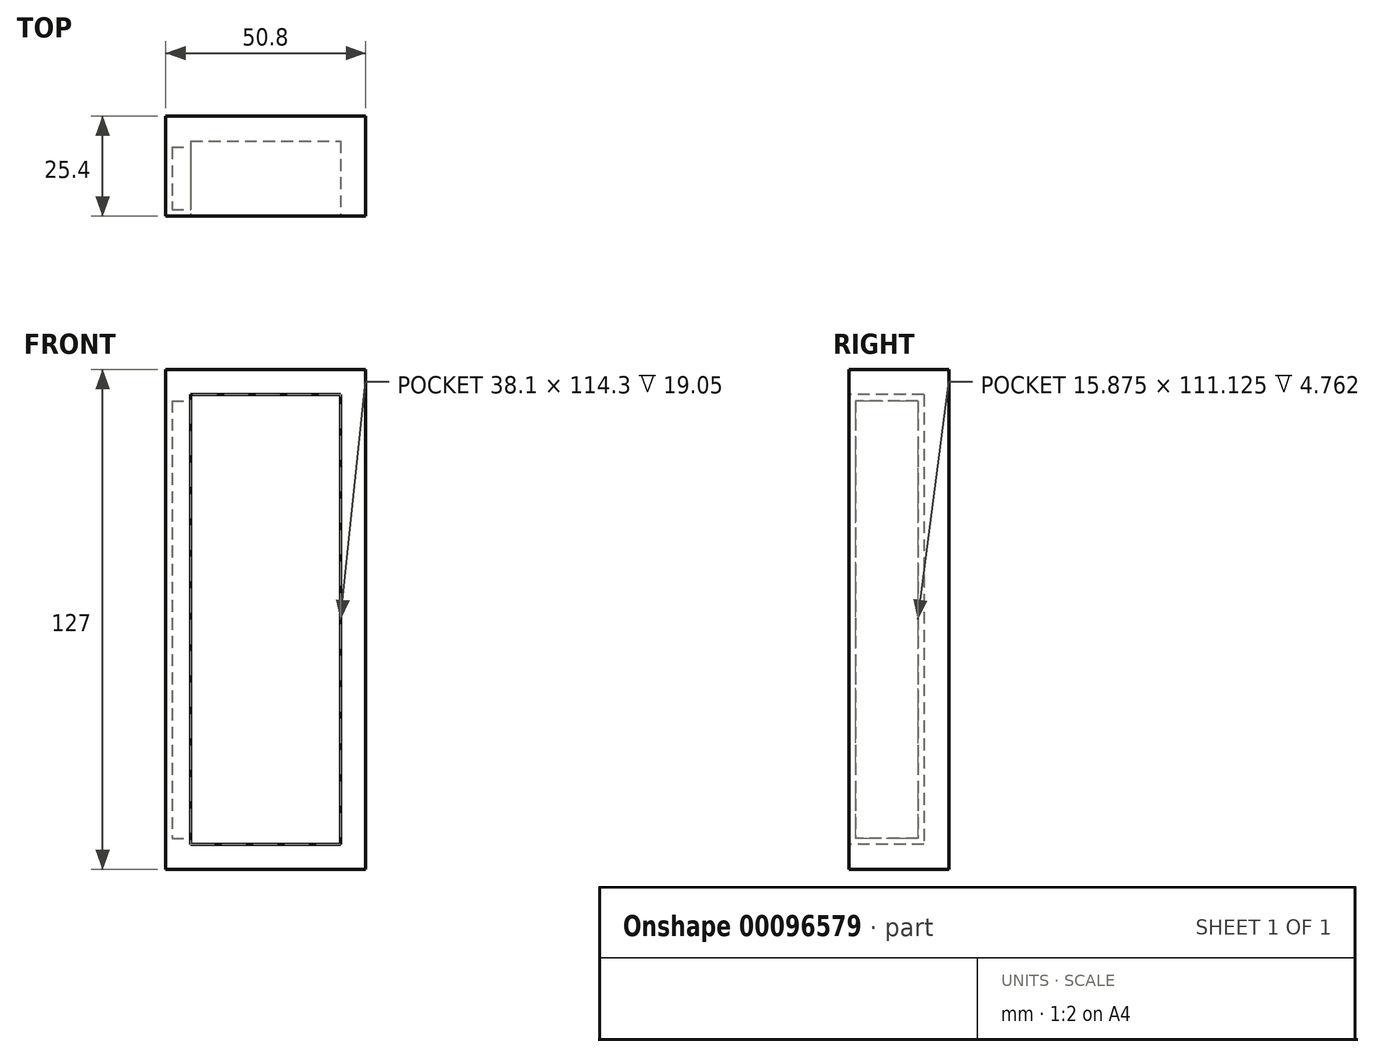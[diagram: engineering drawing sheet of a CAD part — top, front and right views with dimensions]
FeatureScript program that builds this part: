
annotation { "Feature Type Name" : "Feature", "Feature Type Description" : "" }
export const myFeature = defineFeature(function(context is Context, id is Id, definition is map)
    precondition{}
    {
        {
            var Q0;
            Q0=qCreatedBy(makeId("Front.planeOp"),FACE);
            var sketch = newSketch(context, id + "F0", { "sketchPlane" : qUnion([Q0])});
            skLineSegment(sketch, "E0.bottom", {"start": v(-29.1, 68.88) * mm, "end": v(21.7, 68.88) * mm});
            skLineSegment(sketch, "E0.top", {"start": v(-29.1, -58.12) * mm, "end": v(21.7, -58.12) * mm});
            skLineSegment(sketch, "E0.left", {"start": v(-29.1, 68.88) * mm, "end": v(-29.1, -58.12) * mm});
            skLineSegment(sketch, "E0.right", {"start": v(21.7, 68.88) * mm, "end": v(21.7, -58.12) * mm});
            skSolve(sketch);
        }
        {
            var Q0;
            Q0 = qSketchRegion(id + "F0", true);
            extrude(context, id + "F1", {"entities" : qUnion([Q0]), "depth" : 25.4 * mm});
        }
        {
            var Q0;
            Q0=makeQuery(id+"F1.opExtrude","CAP_FACE",FACE,{"disambiguationData":[OSD([sQuery(id+"F0.wireOp",EDGE,"E0.bottom"),sQuery(id+"F0.wireOp",EDGE,"E0.top"),sQuery(id+"F0.wireOp",EDGE,"E0.left"),sQuery(id+"F0.wireOp",EDGE,"E0.right")])],"isStart":false});
            var sketch = newSketch(context, id + "F2", { "sketchPlane" : qUnion([Q0])});
            skLineSegment(sketch, "E1.bottom", {"start": v(-22.76, 62.53) * mm, "end": v(15.34, 62.53) * mm});
            skLineSegment(sketch, "E1.top", {"start": v(-22.76, -51.77) * mm, "end": v(15.34, -51.77) * mm});
            skLineSegment(sketch, "E1.left", {"start": v(-22.76, 62.53) * mm, "end": v(-22.76, -51.77) * mm});
            skLineSegment(sketch, "E1.right", {"start": v(15.34, 62.53) * mm, "end": v(15.34, -51.77) * mm});
            skSolve(sketch);
        }
        {
            var Q0;
            Q0 = qSketchRegion(id + "F2", true);
            extrude(context, id + "F3", {"entities" : qUnion([Q0]), "operationType" : NewBodyOperationType.REMOVE, "oppositeDirection" : true, "depth" : 19.05 * mm});
        }
        {
            var Q0;
            Q0=makeQuery(id+"F3.boolean.opBoolean","COPY",FACE,{"derivedFrom":makeQuery(id+"F3.opExtrude","SWEPT_FACE",FACE,{"disambiguationData":[OSD([sQuery(id+"F2.wireOp",EDGE,"E1.left")])]})});
            var sketch = newSketch(context, id + "F4", { "sketchPlane" : qUnion([Q0])});
            skLineSegment(sketch, "E2.bottom", {"start": v(-7.94, 60.94) * mm, "end": v(-23.81, 60.94) * mm});
            skLineSegment(sketch, "E2.top", {"start": v(-7.94, -50.19) * mm, "end": v(-23.81, -50.19) * mm});
            skLineSegment(sketch, "E2.left", {"start": v(-7.94, 60.94) * mm, "end": v(-7.94, -50.19) * mm});
            skLineSegment(sketch, "E2.right", {"start": v(-23.81, 60.94) * mm, "end": v(-23.81, -50.19) * mm});
            skSolve(sketch);
        }
        {
            var Q0;
            Q0 = qSketchRegion(id + "F4", true);
            extrude(context, id + "F5", {"entities" : qUnion([Q0]), "operationType" : NewBodyOperationType.REMOVE, "oppositeDirection" : true, "depth" : 4.76 * mm});
        }
    });
